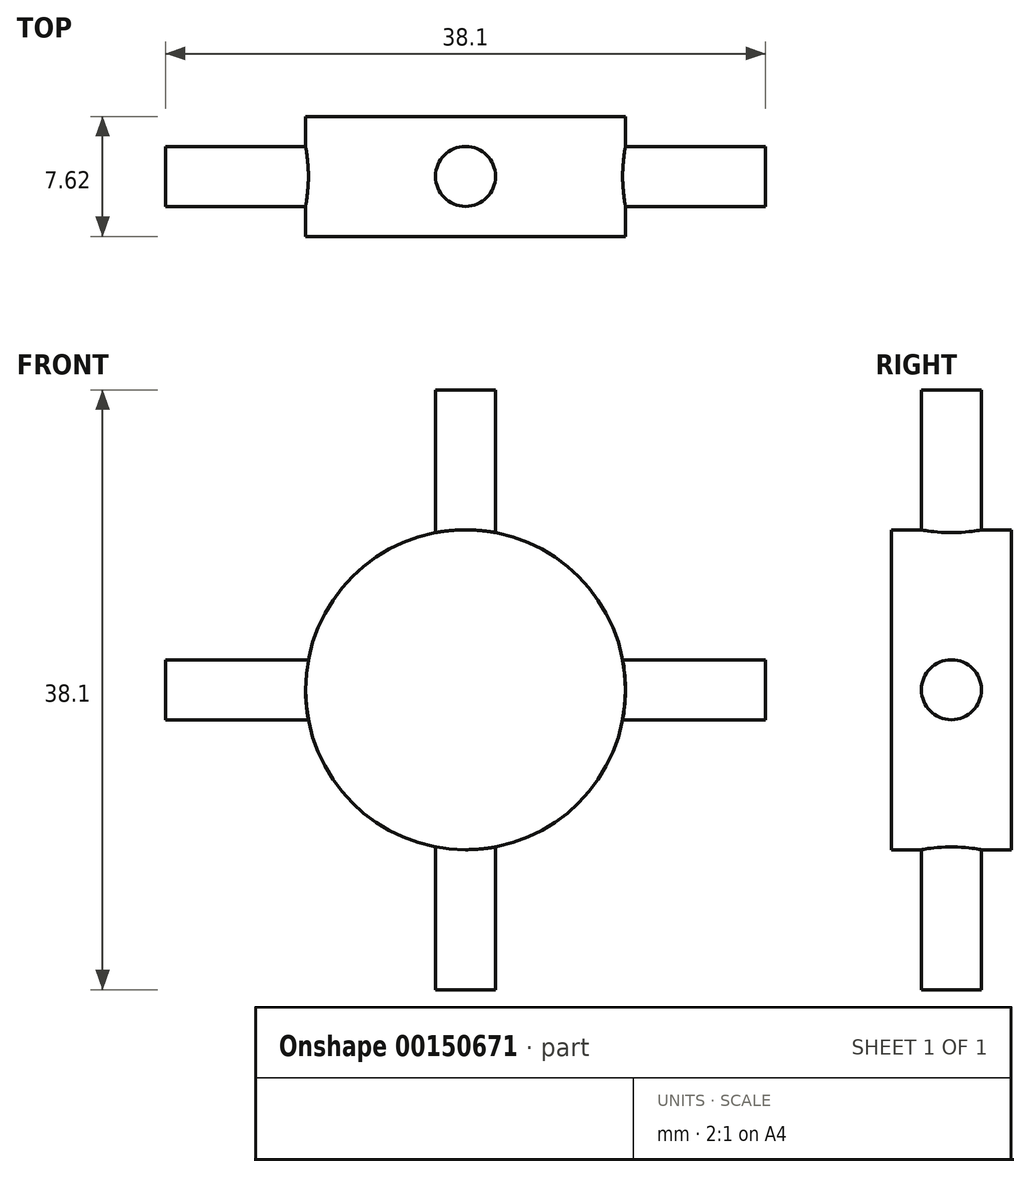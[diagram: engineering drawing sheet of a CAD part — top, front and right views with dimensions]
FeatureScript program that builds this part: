
annotation { "Feature Type Name" : "Feature", "Feature Type Description" : "" }
export const myFeature = defineFeature(function(context is Context, id is Id, definition is map)
    precondition{}
    {
        {
            var Q0;
            Q0=qCreatedBy(makeId("Front.planeOp"),FACE);
            var sketch = newSketch(context, id + "F0", { "sketchPlane" : qUnion([Q0])});
            skCircle(sketch, "E0", {"center": v(0, 0) * mm, "radius": 10.16 * mm});
            skSolve(sketch);
        }
        {
            var Q0;
            Q0=makeQuery(id+"F0.imprint","IMPRINT",FACE,{"disambiguationData":[TD([[makeQuery(id+"F0.imprint","IMPRINT",EDGE,{"derivedFrom":sQuery(id+"F0.wireOp",EDGE,"E0")}),1.0]])]});
            extrude(context, id + "F1", {"entities" : qUnion([Q0]), "endBound" : BoundingType.SYMMETRIC, "depth" : 7.62 * mm});
        }
        {
            var Q0;
            Q0=qCreatedBy(makeId("Top.planeOp"),FACE);
            var sketch = newSketch(context, id + "F2", { "sketchPlane" : qUnion([Q0])});
            skCircle(sketch, "E1", {"center": v(0, 0) * mm, "radius": 1.9 * mm});
            skSolve(sketch);
        }
        {
            var Q0;
            Q0 = qSketchRegion(id + "F2", true);
            extrude(context, id + "F3", {"entities" : qUnion([Q0]), "operationType" : NewBodyOperationType.ADD, "endBound" : BoundingType.SYMMETRIC, "depth" : 38.1 * mm});
        }
        {
            var Q0;
            Q0=qCreatedBy(makeId("Right.planeOp"),FACE);
            var sketch = newSketch(context, id + "F4", { "sketchPlane" : qUnion([Q0])});
            skCircle(sketch, "E2", {"center": v(0, 0) * mm, "radius": 1.9 * mm});
            skSolve(sketch);
        }
        {
            var Q0;
            Q0 = qSketchRegion(id + "F4", true);
            extrude(context, id + "F5", {"entities" : qUnion([Q0]), "operationType" : NewBodyOperationType.ADD, "endBound" : BoundingType.SYMMETRIC, "depth" : 38.1 * mm});
        }
    });
